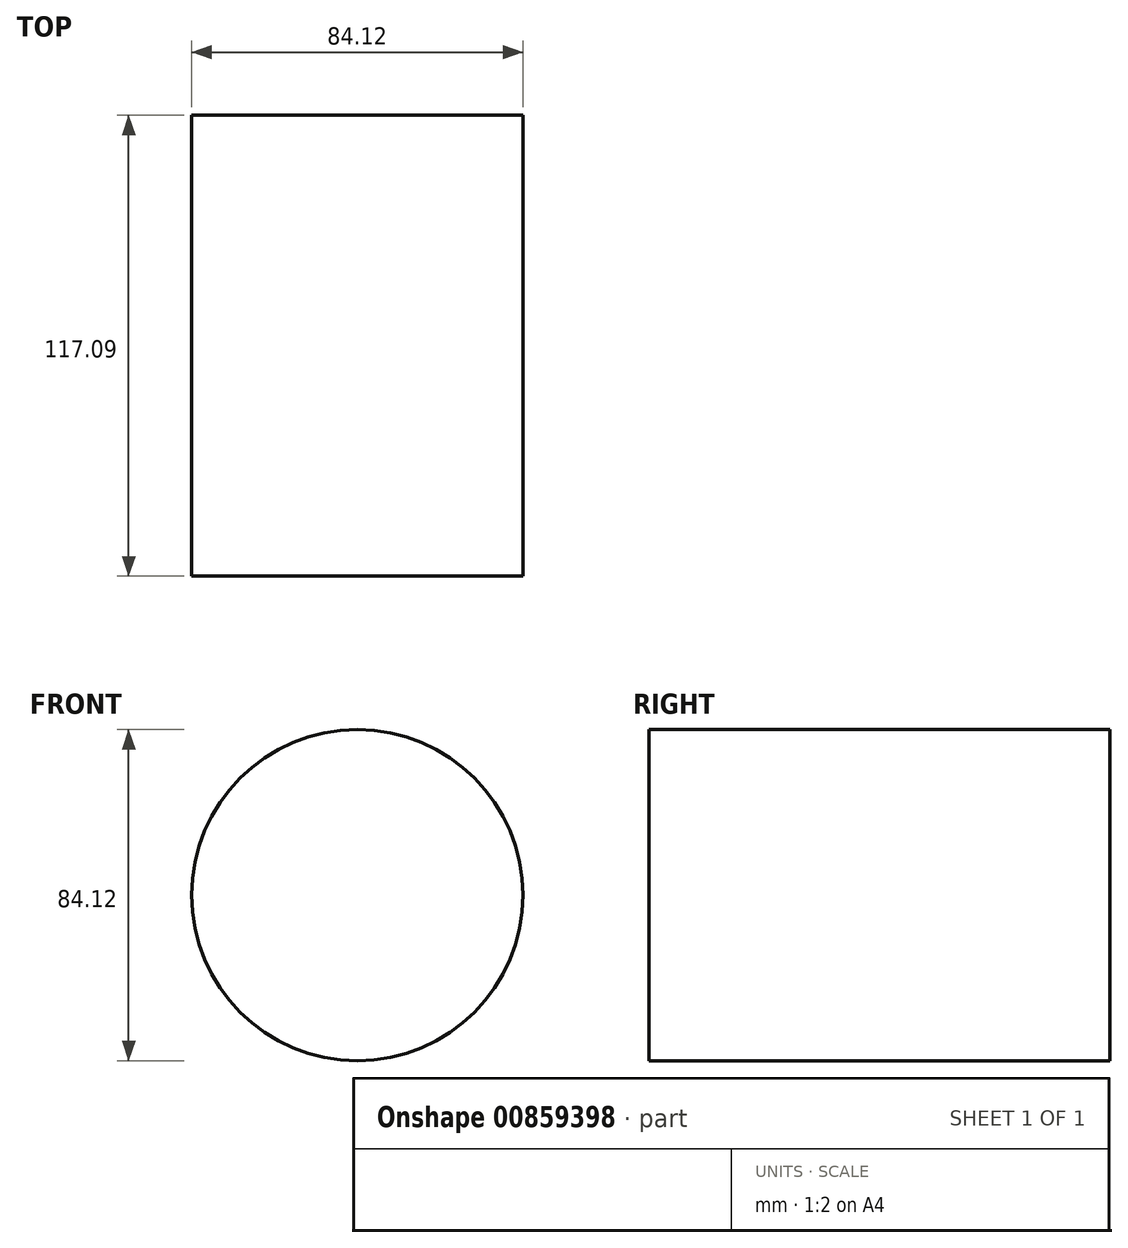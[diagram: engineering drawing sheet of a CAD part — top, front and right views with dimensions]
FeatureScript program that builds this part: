
annotation { "Feature Type Name" : "Feature", "Feature Type Description" : "" }
export const myFeature = defineFeature(function(context is Context, id is Id, definition is map)
    precondition{}
    {
        {
            var Q0;
            Q0=qCreatedBy(makeId("Front.planeOp"),FACE);
            var sketch = newSketch(context, id + "F0", { "sketchPlane" : qUnion([Q0])});
            skCircle(sketch, "E0", {"center": v(0, 0) * mm, "radius": 42.06 * mm});
            skSolve(sketch);
        }
        {
            var Q0;
            Q0=makeQuery(id+"F0.imprint","IMPRINT",FACE,{"disambiguationData":[TD([[makeQuery(id+"F0.imprint","IMPRINT",EDGE,{"derivedFrom":sQuery(id+"F0.wireOp",EDGE,"E0")}),1.0]])]});
            var Q1;
            Q1=sQuery(id+"F0.wireOp",EDGE,"E0");
            extrude(context, id + "F1", {"entities" : qUnion([Q0]), "surfaceEntities" : qUnion([Q1]), "depth" : 117.1 * mm, "offsetDistance" : 25.4 * mm});
        }
    });
